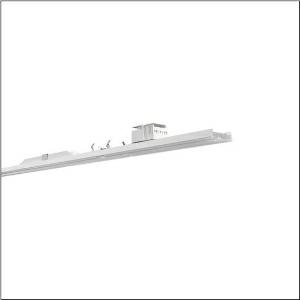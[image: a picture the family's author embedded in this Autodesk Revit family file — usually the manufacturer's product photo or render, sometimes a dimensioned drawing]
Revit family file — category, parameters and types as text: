
# Revit family: licross_r__11_recessed_mo_51tl12cn48xfd_980c
name_source: partatom
category: Lighting Fixtures
units: mm (PartAtom-declared; Revit-internal decimal feet)

## family parameters
Cut with Voids When Loaded = No
Host = Face
Light Source = No
Part Type = Normal
Room Calculation Point = No
Round Connector Dimension = Use Diameter
Shared = No

## types (1)
- --- (1 x LED, 3410 lm, 22.1 W, 4000K)
    Apparent Load = 22 VA
    CIE Flux Codes = 67 92 99 100 100
    Color Rendering = 80
    Color Temperature = 4000K
    Default Elevation = 1800 mm
    Description = Licross® 11 Recessed MOluminaire insert, length: 1.500mm, width: 66mm, height: 67mm, LED rated luminous flux: 8.280lm, light colour: 840, control gear: ON/OFF Multilumen, CLOi, control gear: ECG Multilumen, with plug, 6-pole, with phase selection, mains connection: 220..240V, AC/DC, 0/50..60Hz, without changeover relay, for emergency light function, for central battery installations according to DIN EN 60598-2-22, halogen-free wiring, primary optical cover: cover, of PMMA, light emission: direct distribution, protection rating (complete): IP40, insulation class (complete): insulation class I (protective earthing), certification: CE, ENEC, VDE, protection symbol: D if used in an environment without relevant dust loads with corresponding accessories, permissible ambient temperature for indoor applications: -35..+40°C, standard: EN 60598-2-22, reducing of maximum allowable ambient temperature of 5°C with ceiling mounting, corresponds to IFS (International Featured Standards) requirements for safety and quality in the food industry, packaging unit: 1 piece
    Height = 58 mm
    Lamp = 1 x LED
    Lamp Light Flux = 3410 lm
    Lamp Power = 22.1 W
    Lamp count = 1
    Length = 1500 mm
    Luminous efficacy = 154 lm/W
    Manufacturer = Siteco
    ModVariant = No
    Model = 51TL12CN48XFD
    Mounting Place = Ceiling
    Mounting Type = Pendant
    Number of Poles = 1
    OnlyDefault = Yes
    Power Factor = 1
    Product Name = Licross® 11 Recessed MO
    Product group = luminaire insert
    ProductGroupID = 902
    Protection Class = Protection class I
    Protection Degree = IP 40
    RLX_Detail_Level = 1
    RlxData = <blob elided: 20453 chars, md5=3c6efafb>
    Socket = socket
    Standby Power = 0 W
    System Light Flux = 3410 lm
    System Power = 22 W
    Type Comments = : DC mode (central or group accumulator) initial emergency light level
    Type Image = l_1266722.jpg
    URL = http://relux.com
    VarID = @adj_134407
    Voltage = 0 V
    Weight = 0.00 kg
    Width = 66 mm

## geometry (parser evidence)
native form markers: Blend x4, Sweep x11
no freeform markers — native parametric forms only
